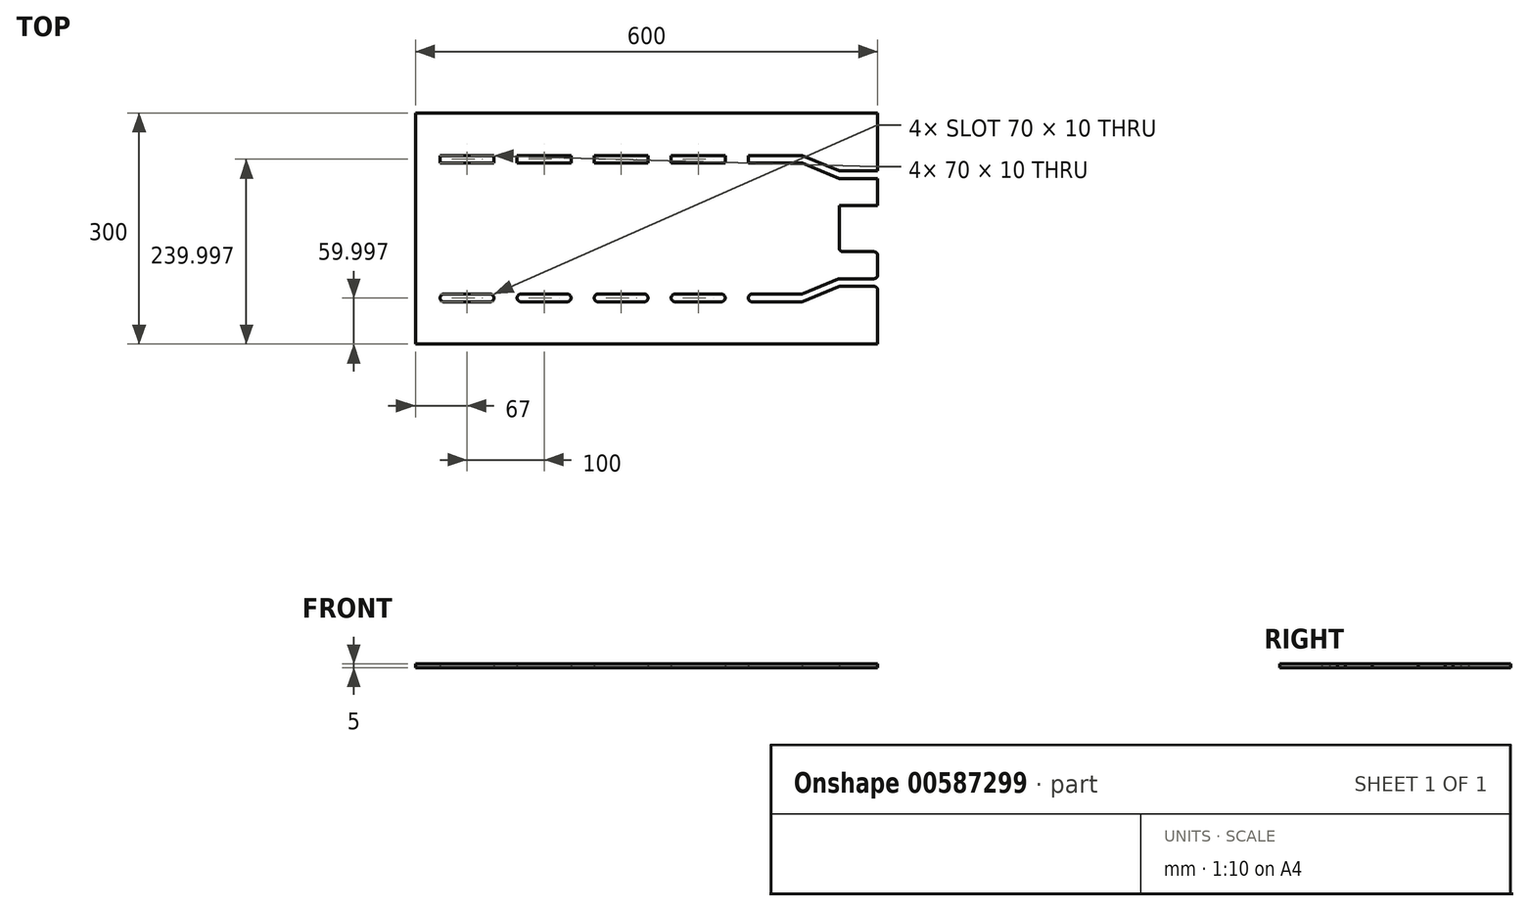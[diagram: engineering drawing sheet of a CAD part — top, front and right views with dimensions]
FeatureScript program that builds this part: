
annotation { "Feature Type Name" : "Feature", "Feature Type Description" : "" }
export const myFeature = defineFeature(function(context is Context, id is Id, definition is map)
    precondition{}
    {
        {
            var Q0;
            Q0=qCreatedBy(makeId("Top.planeOp"),FACE);
            var sketch = newSketch(context, id + "F0", { "sketchPlane" : qUnion([Q0])});
            skLineSegment(sketch, "E0.bottom", {"start": v(-300, 149.23) * mm, "end": v(300, 149.23) * mm});
            skLineSegment(sketch, "E0.top", {"start": v(-300, -150.77) * mm, "end": v(300, -150.77) * mm});
            skLineSegment(sketch, "E0.left", {"start": v(-300, 149.23) * mm, "end": v(-300, -150.77) * mm});
            skLineSegment(sketch, "E0.right", {"start": v(300, 149.23) * mm, "end": v(300, -150.77) * mm});
            skLineSegment(sketch, "E1", {"start": v(0, 149.23) * mm, "end": v(0, -150.77) * mm, "construction": true});
            skLineSegment(sketch, "E2", {"start": v(-300, -0.77) * mm, "end": v(300, -0.77) * mm, "construction": true});
            skLineSegment(sketch, "E3.bottom", {"start": v(300, -30.77) * mm, "end": v(250, -30.77) * mm});
            skLineSegment(sketch, "E3.top", {"start": v(300, 29.23) * mm, "end": v(250, 29.23) * mm});
            skLineSegment(sketch, "E3.left", {"start": v(300, -30.77) * mm, "end": v(300, 29.23) * mm});
            skLineSegment(sketch, "E3.right", {"start": v(250, -30.77) * mm, "end": v(250, 29.23) * mm});
            skPoint(sketch, "E3.middle", {"position": v(275, -0.77) * mm});
            skLineSegment(sketch, "E4", {"start": v(250, -30.77) * mm, "end": v(250, -150.77) * mm, "construction": true});
            skLineSegment(sketch, "E5", {"start": v(250, 29.23) * mm, "end": v(250, 149.23) * mm, "construction": true});
            skLineSegment(sketch, "E6", {"start": v(250, -90.77) * mm, "end": v(-300, -90.77) * mm, "construction": true});
            skLineSegment(sketch, "E7.bottom", {"start": v(-268, -85.77) * mm, "end": v(-198, -85.77) * mm});
            skLineSegment(sketch, "E7.top", {"start": v(-268, -95.77) * mm, "end": v(-198, -95.77) * mm});
            skLineSegment(sketch, "E7.left", {"start": v(-268, -85.77) * mm, "end": v(-268, -95.77) * mm});
            skLineSegment(sketch, "E7.right", {"start": v(-198, -85.77) * mm, "end": v(-198, -95.77) * mm});
            skPoint(sketch, "E7.middle", {"position": v(-233, -90.77) * mm});
            skLineSegment(sketch, "E8", {"start": v(-300, -90.77) * mm, "end": v(-268, -90.77) * mm, "construction": true});
            skLineSegment(sketch, "E9.1.0.0", {"start": v(-168, -95.77) * mm, "end": v(-98, -95.77) * mm});
            skLineSegment(sketch, "E9.1.0.1", {"start": v(-168, -85.77) * mm, "end": v(-98, -85.77) * mm});
            skLineSegment(sketch, "E9.1.0.2", {"start": v(-98, -85.77) * mm, "end": v(-98, -95.77) * mm});
            skPoint(sketch, "E9.1.0.3", {"position": v(-133, -90.77) * mm});
            skLineSegment(sketch, "E9.1.0.4", {"start": v(-168, -85.77) * mm, "end": v(-168, -95.77) * mm});
            skLineSegment(sketch, "E9.2.0.0", {"start": v(-68, -95.77) * mm, "end": v(2, -95.77) * mm});
            skLineSegment(sketch, "E9.2.0.1", {"start": v(-68, -85.77) * mm, "end": v(2, -85.77) * mm});
            skLineSegment(sketch, "E9.2.0.2", {"start": v(2, -85.77) * mm, "end": v(2, -95.77) * mm});
            skPoint(sketch, "E9.2.0.3", {"position": v(-33, -90.77) * mm});
            skLineSegment(sketch, "E9.2.0.4", {"start": v(-68, -85.77) * mm, "end": v(-68, -95.77) * mm});
            skLineSegment(sketch, "E9.3.0.0", {"start": v(32, -95.77) * mm, "end": v(102, -95.77) * mm});
            skLineSegment(sketch, "E9.3.0.1", {"start": v(32, -85.77) * mm, "end": v(102, -85.77) * mm});
            skLineSegment(sketch, "E9.3.0.2", {"start": v(102, -85.77) * mm, "end": v(102, -95.77) * mm});
            skPoint(sketch, "E9.3.0.3", {"position": v(67, -90.77) * mm});
            skLineSegment(sketch, "E9.3.0.4", {"start": v(32, -85.77) * mm, "end": v(32, -95.77) * mm});
            skLineSegment(sketch, "E9.4.0.0", {"start": v(132, -95.77) * mm, "end": v(202, -95.77) * mm});
            skLineSegment(sketch, "E9.4.0.1", {"start": v(132, -85.77) * mm, "end": v(202, -85.77) * mm});
            skLineSegment(sketch, "E9.4.0.2", {"start": v(202, -85.77) * mm, "end": v(202, -95.77) * mm});
            skPoint(sketch, "E9.4.0.3", {"position": v(167, -90.77) * mm});
            skLineSegment(sketch, "E9.4.0.4", {"start": v(132, -85.77) * mm, "end": v(132, -95.77) * mm});
            skLineSegment(sketch, "E9.direction1", {"start": v(-268, -95.77) * mm, "end": v(-168, -95.77) * mm, "construction": true});
            skLineSegment(sketch, "E10", {"start": v(-300, 89.23) * mm, "end": v(-270, 89.23) * mm, "construction": true});
            skLineSegment(sketch, "E11", {"start": v(250, -30.77) * mm, "end": v(250, -70.77) * mm, "construction": true});
            skLineSegment(sketch, "E12", {"start": v(250, -70.77) * mm, "end": v(300, -70.77) * mm, "construction": true});
            skLineSegment(sketch, "E13.bottom", {"start": v(250, -65.77) * mm, "end": v(300, -65.77) * mm});
            skLineSegment(sketch, "E13.top", {"start": v(250, -75.77) * mm, "end": v(300, -75.77) * mm});
            skLineSegment(sketch, "E13.left", {"start": v(250, -65.77) * mm, "end": v(250, -75.77) * mm});
            skLineSegment(sketch, "E13.right", {"start": v(300, -65.77) * mm, "end": v(300, -75.77) * mm});
            skPoint(sketch, "E13.middle", {"position": v(275, -70.77) * mm});
            skLineSegment(sketch, "E14", {"start": v(250, -75.77) * mm, "end": v(202, -95.77) * mm});
            skLineSegment(sketch, "E15", {"start": v(250, -65.77) * mm, "end": v(202, -85.77) * mm});
            skLineSegment(sketch, "E16.MirrorCS", {"start": v(250, 74.23) * mm, "end": v(300, 74.23) * mm});
            skLineSegment(sketch, "E17.MirrorCS", {"start": v(250, 64.23) * mm, "end": v(300, 64.23) * mm});
            skLineSegment(sketch, "E18.MirrorCS", {"start": v(250, 64.23) * mm, "end": v(202, 84.23) * mm});
            skLineSegment(sketch, "E19.MirrorCS", {"start": v(250, 74.23) * mm, "end": v(202, 94.23) * mm});
            skLineSegment(sketch, "E20.MirrorCS", {"start": v(202, 84.23) * mm, "end": v(202, 94.23) * mm});
            skLineSegment(sketch, "E21.MirrorCS", {"start": v(-268, 84.23) * mm, "end": v(-268, 94.23) * mm});
            skLineSegment(sketch, "E22.MirrorCS", {"start": v(-168, 84.23) * mm, "end": v(-168, 94.23) * mm});
            skLineSegment(sketch, "E23.MirrorCS", {"start": v(2, 84.23) * mm, "end": v(2, 94.23) * mm});
            skLineSegment(sketch, "E24.MirrorCS", {"start": v(102, 84.23) * mm, "end": v(102, 94.23) * mm});
            skLineSegment(sketch, "E25.MirrorCS", {"start": v(-198, 84.23) * mm, "end": v(-198, 94.23) * mm});
            skLineSegment(sketch, "E26.MirrorCS", {"start": v(-98, 84.23) * mm, "end": v(-98, 94.23) * mm});
            skLineSegment(sketch, "E27.MirrorCS", {"start": v(132, 84.23) * mm, "end": v(132, 94.23) * mm});
            skLineSegment(sketch, "E28.MirrorCS", {"start": v(32, 84.23) * mm, "end": v(32, 94.23) * mm});
            skLineSegment(sketch, "E29.MirrorCS", {"start": v(-68, 84.23) * mm, "end": v(-68, 94.23) * mm});
            skLineSegment(sketch, "E30.MirrorCS", {"start": v(-268, 94.23) * mm, "end": v(-198, 94.23) * mm});
            skPoint(sketch, "E31.MirrorP", {"position": v(-133, 89.23) * mm});
            skPoint(sketch, "E32.MirrorP", {"position": v(-233, 89.23) * mm});
            skLineSegment(sketch, "E33.MirrorCS", {"start": v(-68, 94.23) * mm, "end": v(2, 94.23) * mm});
            skPoint(sketch, "E34.MirrorP", {"position": v(167, 89.23) * mm});
            skLineSegment(sketch, "E35.MirrorCS", {"start": v(132, 94.23) * mm, "end": v(202, 94.23) * mm});
            skLineSegment(sketch, "E36.MirrorCS", {"start": v(132, 84.23) * mm, "end": v(202, 84.23) * mm});
            skLineSegment(sketch, "E37.MirrorCS", {"start": v(-68, 84.23) * mm, "end": v(2, 84.23) * mm});
            skLineSegment(sketch, "E38.MirrorCS", {"start": v(-168, 94.23) * mm, "end": v(-98, 94.23) * mm});
            skLineSegment(sketch, "E39.MirrorCS", {"start": v(32, 84.23) * mm, "end": v(102, 84.23) * mm});
            skLineSegment(sketch, "E40.MirrorCS", {"start": v(-268, 94.23) * mm, "end": v(-168, 94.23) * mm, "construction": true});
            skPoint(sketch, "E41.MirrorP", {"position": v(-33, 89.23) * mm});
            skLineSegment(sketch, "E42.MirrorCS", {"start": v(32, 94.23) * mm, "end": v(102, 94.23) * mm});
            skLineSegment(sketch, "E43.MirrorCS", {"start": v(-168, 84.23) * mm, "end": v(-98, 84.23) * mm});
            skPoint(sketch, "E44.MirrorP", {"position": v(67, 89.23) * mm});
            skLineSegment(sketch, "E45.MirrorCS", {"start": v(-268, 84.23) * mm, "end": v(-198, 84.23) * mm});
            skSolve(sketch);
        }
        {
            var Q0;
            {var subQ10=sQuery(id+"F0.wireOp",EDGE,"E0.bottom");Q0=makeQuery(id+"F0.imprint","IMPRINT",FACE,{"disambiguationData":[TD([[makeQuery(id+"F0.imprint","IMPRINT",EDGE,{"derivedFrom":subQ10}),-1.0]])]});}
            extrude(context, id + "F1", {"entities" : qUnion([Q0]), "depth" : 5 * mm, "offsetDistance" : 25 * mm});
        }
        {
            var Q0;
            Q0=makeQuery(id+"F1.opExtrude","SWEPT_EDGE",EDGE,{"disambiguationData":[OSD([sQuery(id+"F0.wireOp",EDGE,"E9.4.0.0"),sQuery(id+"F0.wireOp",EDGE,"E9.4.0.4")])]});
            var Q1;
            Q1=makeQuery(id+"F1.opExtrude","SWEPT_EDGE",EDGE,{"disambiguationData":[OSD([sQuery(id+"F0.wireOp",EDGE,"E9.3.0.0"),sQuery(id+"F0.wireOp",EDGE,"E9.3.0.4")])]});
            var Q2;
            Q2=makeQuery(id+"F1.opExtrude","SWEPT_EDGE",EDGE,{"disambiguationData":[OSD([sQuery(id+"F0.wireOp",EDGE,"E9.2.0.0"),sQuery(id+"F0.wireOp",EDGE,"E9.2.0.4")])]});
            var Q3;
            Q3=makeQuery(id+"F1.opExtrude","SWEPT_EDGE",EDGE,{"disambiguationData":[OSD([sQuery(id+"F0.wireOp",EDGE,"E9.4.0.0"),sQuery(id+"F0.wireOp",EDGE,"E9.4.0.2"),sQuery(id+"F0.wireOp",EDGE,"E14")])]});
            var Q4;
            Q4=makeQuery(id+"F1.opExtrude","SWEPT_EDGE",EDGE,{"disambiguationData":[OSD([sQuery(id+"F0.wireOp",EDGE,"E13.top"),sQuery(id+"F0.wireOp",EDGE,"E13.left"),sQuery(id+"F0.wireOp",EDGE,"E14")])]});
            var Q5;
            Q5=makeQuery(id+"F1.opExtrude","SWEPT_EDGE",EDGE,{"disambiguationData":[OSD([sQuery(id+"F0.wireOp",EDGE,"E9.1.0.0"),sQuery(id+"F0.wireOp",EDGE,"E9.1.0.4")])]});
            var Q6;
            Q6=makeQuery(id+"F1.opExtrude","SWEPT_EDGE",EDGE,{"disambiguationData":[OSD([sQuery(id+"F0.wireOp",EDGE,"E7.top"),sQuery(id+"F0.wireOp",EDGE,"E7.left")])]});
            var Q7;
            Q7=makeQuery(id+"F1.opExtrude","SWEPT_EDGE",EDGE,{"disambiguationData":[OSD([sQuery(id+"F0.wireOp",EDGE,"E0.right"),sQuery(id+"F0.wireOp",EDGE,"E13.top"),sQuery(id+"F0.wireOp",EDGE,"E13.right")])]});
            var Q8;
            Q8=makeQuery(id+"F1.opExtrude","SWEPT_EDGE",EDGE,{"disambiguationData":[OSD([sQuery(id+"F0.wireOp",EDGE,"E0.right"),sQuery(id+"F0.wireOp",EDGE,"E13.bottom"),sQuery(id+"F0.wireOp",EDGE,"E13.right")])]});
            var Q9;
            Q9=makeQuery(id+"F1.opExtrude","SWEPT_EDGE",EDGE,{"disambiguationData":[OSD([sQuery(id+"F0.wireOp",EDGE,"E0.right"),sQuery(id+"F0.wireOp",EDGE,"E3.bottom"),sQuery(id+"F0.wireOp",EDGE,"E3.left")])]});
            var Q10;
            Q10=makeQuery(id+"F1.opExtrude","SWEPT_EDGE",EDGE,{"disambiguationData":[OSD([sQuery(id+"F0.wireOp",EDGE,"E3.bottom"),sQuery(id+"F0.wireOp",EDGE,"E3.right")])]});
            var Q11;
            Q11=makeQuery(id+"F1.opExtrude","SWEPT_EDGE",EDGE,{"disambiguationData":[OSD([sQuery(id+"F0.wireOp",EDGE,"E13.bottom"),sQuery(id+"F0.wireOp",EDGE,"E13.left"),sQuery(id+"F0.wireOp",EDGE,"E15")])]});
            var Q12;
            Q12=makeQuery(id+"F1.opExtrude","SWEPT_EDGE",EDGE,{"disambiguationData":[OSD([sQuery(id+"F0.wireOp",EDGE,"E9.4.0.1"),sQuery(id+"F0.wireOp",EDGE,"E9.4.0.2"),sQuery(id+"F0.wireOp",EDGE,"E15")])]});
            var Q13;
            Q13=makeQuery(id+"F1.opExtrude","SWEPT_EDGE",EDGE,{"disambiguationData":[OSD([sQuery(id+"F0.wireOp",EDGE,"E9.4.0.1"),sQuery(id+"F0.wireOp",EDGE,"E9.4.0.4")])]});
            var Q14;
            Q14=makeQuery(id+"F1.opExtrude","SWEPT_EDGE",EDGE,{"disambiguationData":[OSD([sQuery(id+"F0.wireOp",EDGE,"E9.3.0.1"),sQuery(id+"F0.wireOp",EDGE,"E9.3.0.2")])]});
            var Q15;
            Q15=makeQuery(id+"F1.opExtrude","SWEPT_EDGE",EDGE,{"disambiguationData":[OSD([sQuery(id+"F0.wireOp",EDGE,"E9.2.0.1"),sQuery(id+"F0.wireOp",EDGE,"E9.2.0.2")])]});
            var Q16;
            Q16=makeQuery(id+"F1.opExtrude","SWEPT_EDGE",EDGE,{"disambiguationData":[OSD([sQuery(id+"F0.wireOp",EDGE,"E9.1.0.1"),sQuery(id+"F0.wireOp",EDGE,"E9.1.0.2")])]});
            var Q17;
            Q17=makeQuery(id+"F1.opExtrude","SWEPT_EDGE",EDGE,{"disambiguationData":[OSD([sQuery(id+"F0.wireOp",EDGE,"E7.bottom"),sQuery(id+"F0.wireOp",EDGE,"E7.right")])]});
            var Q18;
            Q18=makeQuery(id+"F1.opExtrude","SWEPT_EDGE",EDGE,{"disambiguationData":[OSD([sQuery(id+"F0.wireOp",EDGE,"E9.3.0.1"),sQuery(id+"F0.wireOp",EDGE,"E9.3.0.4")])]});
            var Q19;
            Q19=makeQuery(id+"F1.opExtrude","SWEPT_EDGE",EDGE,{"disambiguationData":[OSD([sQuery(id+"F0.wireOp",EDGE,"E9.2.0.1"),sQuery(id+"F0.wireOp",EDGE,"E9.2.0.4")])]});
            var Q20;
            Q20=makeQuery(id+"F1.opExtrude","SWEPT_EDGE",EDGE,{"disambiguationData":[OSD([sQuery(id+"F0.wireOp",EDGE,"E9.1.0.1"),sQuery(id+"F0.wireOp",EDGE,"E9.1.0.4")])]});
            var Q21;
            Q21=makeQuery(id+"F1.opExtrude","SWEPT_EDGE",EDGE,{"disambiguationData":[OSD([sQuery(id+"F0.wireOp",EDGE,"E7.bottom"),sQuery(id+"F0.wireOp",EDGE,"E7.left")])]});
            var Q22;
            Q22=makeQuery(id+"F1.opExtrude","SWEPT_EDGE",EDGE,{"disambiguationData":[OSD([sQuery(id+"F0.wireOp",EDGE,"E9.3.0.0"),sQuery(id+"F0.wireOp",EDGE,"E9.3.0.2")])]});
            var Q23;
            Q23=makeQuery(id+"F1.opExtrude","SWEPT_EDGE",EDGE,{"disambiguationData":[OSD([sQuery(id+"F0.wireOp",EDGE,"E9.2.0.0"),sQuery(id+"F0.wireOp",EDGE,"E9.2.0.2")])]});
            var Q24;
            Q24=makeQuery(id+"F1.opExtrude","SWEPT_EDGE",EDGE,{"disambiguationData":[OSD([sQuery(id+"F0.wireOp",EDGE,"E9.1.0.0"),sQuery(id+"F0.wireOp",EDGE,"E9.1.0.2")])]});
            var Q25;
            Q25=makeQuery(id+"F1.opExtrude","SWEPT_EDGE",EDGE,{"disambiguationData":[OSD([sQuery(id+"F0.wireOp",EDGE,"E7.top"),sQuery(id+"F0.wireOp",EDGE,"E7.right")])]});
            fillet(context, id + "F2", {"entities" : qUnion([Q0, Q1, Q2, Q3, Q4, Q5, Q6, Q7, Q8, Q9, Q10, Q11, Q12, Q13, Q14, Q15, Q16, Q17, Q18, Q19, Q20, Q21, Q22, Q23, Q24, Q25]), "radius" : 5 * mm, "tangentPropagation" : true, "allowEdgeOverflow" : false});
        }
    });
